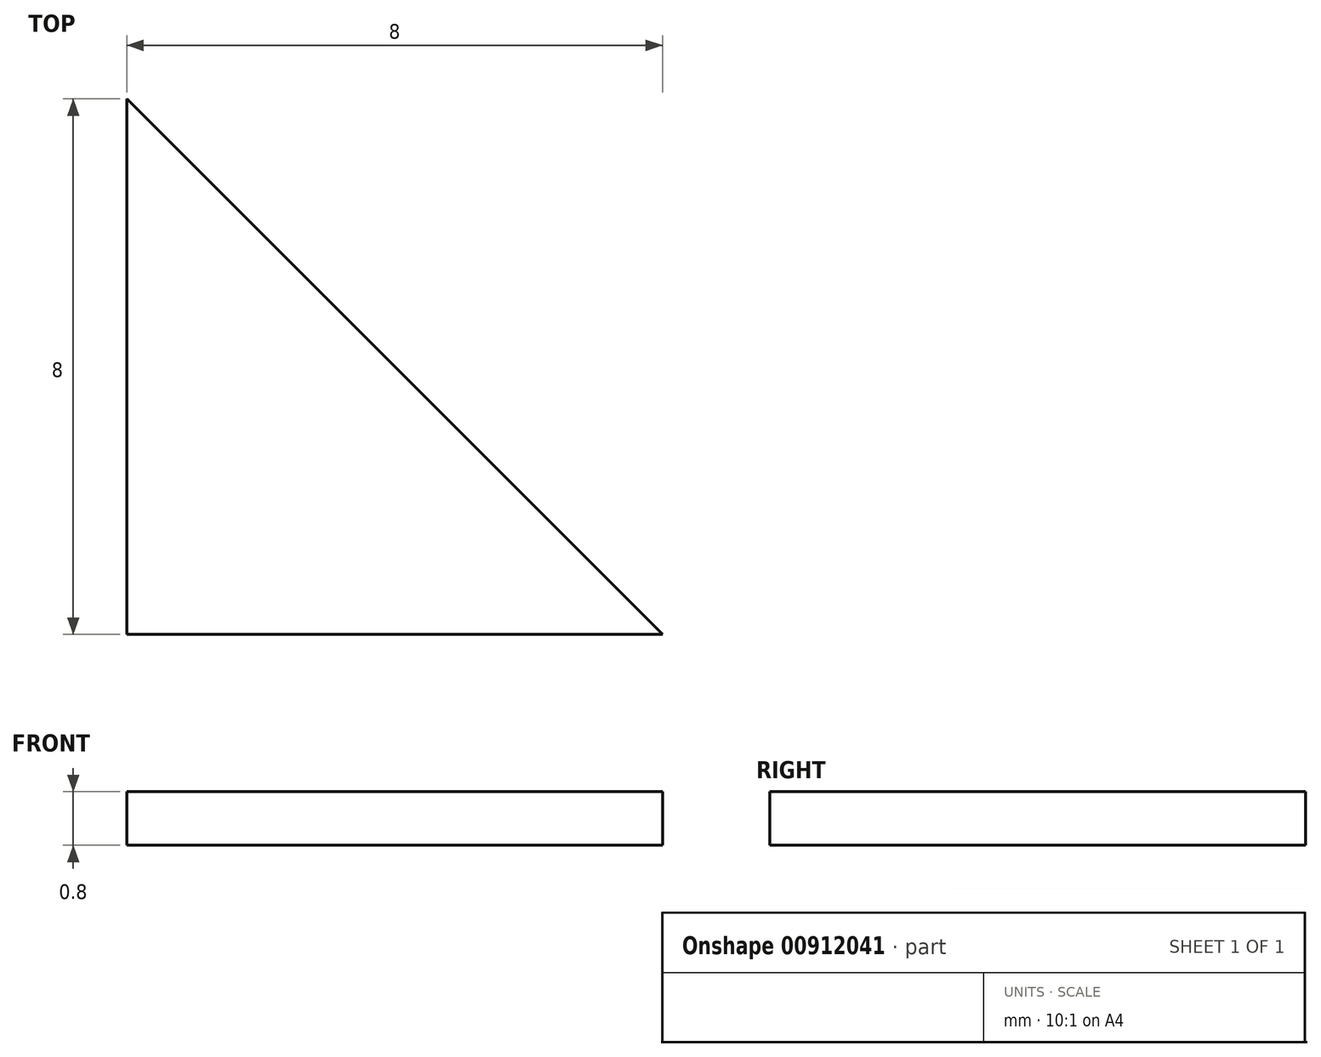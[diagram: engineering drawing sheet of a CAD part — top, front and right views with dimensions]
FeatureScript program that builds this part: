
annotation { "Feature Type Name" : "Feature", "Feature Type Description" : "" }
export const myFeature = defineFeature(function(context is Context, id is Id, definition is map)
    precondition{}
    {
        {
            var Q0;
            Q0=qCreatedBy(makeId("Top.planeOp"),FACE);
            var sketch = newSketch(context, id + "F0", { "sketchPlane" : qUnion([Q0])});
            skLineSegment(sketch, "E0", {"start": v(0, 0) * mm, "end": v(8, 0) * mm});
            skLineSegment(sketch, "E1", {"start": v(8, 0) * mm, "end": v(0, 8) * mm});
            skLineSegment(sketch, "E2", {"start": v(0, 8) * mm, "end": v(0, 0) * mm});
            skSolve(sketch);
        }
        {
            var Q0;
            Q0=makeQuery(id+"F0.imprint","IMPRINT",FACE,{"disambiguationData":[TD([[makeQuery(id+"F0.imprint","IMPRINT",EDGE,{"derivedFrom":sQuery(id+"F0.wireOp",EDGE,"E0")}),1.0]])]});
            extrude(context, id + "F1", {"entities" : qUnion([Q0]), "depth" : .8 * mm, "offsetDistance" : 25 * mm});
        }
    });
